# Revit family: Hager TPN DB IP65 Metal v2
name_source: partatom
category: Electrical Equipment
revit_build: Autodesk Revit 2013 (Build: 20120221_2030(x64)
units: mm (PartAtom-declared; Revit-internal decimal feet)

## types (5) — shared parameters
Busbar Rating = 125 A
CE Approval = Yes
Colour = RAL7035 Light Grey
Default Elevation = 1200 mm
Door Type = Single Plain Door
Enclosure Rating = IP65
Frequency = 50 Hz
Location = Indoors
Location of Manufacturer = Telford, TF1 7FT
MCB Rating = 63 A
Mains Type = 3 phase
Manufacturer = Hager UK Ltd
Manufacturer Website = www.hager.co.uk
Neutral Rating = 100.00%
Number of Poles = 3
Overall Height = 300 mm  [stored 0.984252 ft]
Overall Width = 600 mm  [stored 1.9685 ft]
Packaging Recyclable = Yes
Packaging Weight = 2.00 kg
Pollution Degree = 2
Product Range = Invicta 3 TPN DB Type B IP65 Metal
Reference Standard = BS EN 61439-3
Revision = 2
Supply Phase = 1,3
URL = www.hager.co.uk
Ui Rating = 690 V
Uimp Rating = 4000 V
Voltage = 415
Warranty ID = 24 Months
zero-valued in all types: Door

## per-type parameters (varying)
| type | Description | EAN | Hager Catalogue Ref | Max #3 Pole Breakers | Model | Outging Ways (TP) | Product Description | Product Literature | Product Weight |
| TPN DB 125A 04 Way IP65 Metal | JK1 TPN B Board 4x 63A TP Ways DB IP65 Metal | 5015652251484 | JK104BD | 4 | JK104BD | 4 | JK1 TPN B Board 4x 63A TP Ways DB IP65 Metal | www.hager.co.uk/?artnr=JK104BD | 33.10 kg |
| TPN DB 125A 06 Way IP65 Metal | JK1 TPN B Board 6x 63A TP Ways DB IP65 Metal | 5015652251552 | JK106BD | 6 | JK106BD | 6 | JK1 TPN B Board 6x 63A TP Ways DB IP65 Metal | www.hager.co.uk/?artnr=JK1046D | 33.10 kg |
| TPN DB 125A 08 Way IP65 Metal | JK1 TPN B Board 8x 63A TP Ways DB IP65 Metal | 5015652251620 | JK108BD | 8 | JK108BD | 8 | JK1 TPN B Board 8x 63A TP Ways DB IP65 Metal | www.hager.co.uk/?artnr=JK108BD | 34.00 kg |
| TPN DB 125A 12 Way IP65 Metal | JK1 TPN B Board 12x 63A TP Ways DB IP65 Metal | 5015652251750 | JK112BD | 12 | JK112BD | 12 | JK1 TPN B Board 12x 63A TP Ways DB IP65 Metal | www.hager.co.uk/?artnr=JK112BD | 40.00 kg |
| TPN DB 125A 16 Way IP65 Metal | JK1 TPN B Board 16x 63A TP Ways DB IP65 Metal | 5015652251811 | JK116BD | 16 | JK116BD | 16 | JK1 TPN B Board 16x 63A TP Ways DB IP65 Metal | www.hager.co.uk/?artnr=JK116BD | 33.10 kg |

note: [stored X ft] marks values corroborated as IEEE doubles in the binary element streams (Revit-internal decimal feet)

## geometry (parser evidence)
native form markers: Sweep x2
no freeform markers — native parametric forms only
